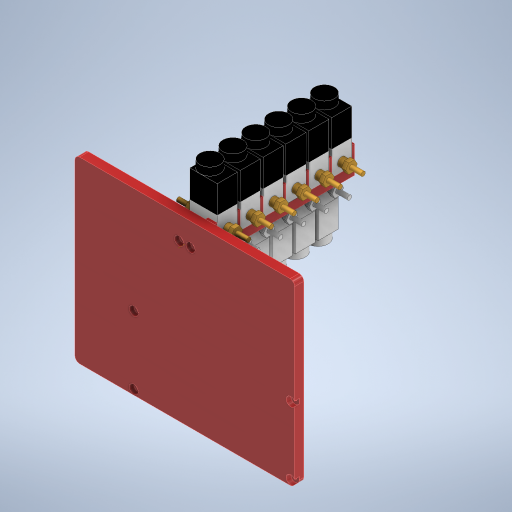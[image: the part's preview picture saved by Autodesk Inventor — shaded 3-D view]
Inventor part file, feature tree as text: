
AUTODESK INVENTOR PART (.ipt)
format: ipt  version: 2024.2 (Build 282272000, 272)  size: 1,256,960 bytes
history: native  units: mm
features: other x37, extrude x15, sketch x13, projected_geometry x11, mirror x2, pattern_linear x2, pattern_circular x2, plane x1, chamfer x1, fillet x1
ambient origin geometry x8: Origin, YZ Plane, XZ Plane, XY Plane, X Axis, Y Axis, Z Axis, Center Point
bodies: Solid6 (feature_tree), Solid8 (feature_tree), Solid11 (feature_tree), Solid14 (feature_tree), Solid17 (feature_tree), Solid20 (feature_tree), Solid7 (feature_tree), Solid10 (feature_tree), Solid13 (feature_tree), Solid16 (feature_tree), Solid19 (feature_tree), Solid9 (feature_tree), Solid12 (feature_tree), Solid15 (feature_tree), Solid18 (feature_tree), Solid21 (feature_tree), Solid48 (feature_tree), Solid53 (feature_tree), Solid47 (feature_tree), Solid52 (feature_tree), Solid46 (feature_tree), Solid51 (feature_tree), Solid45 (feature_tree), Solid50 (feature_tree), Solid44 (feature_tree), Solid49 (feature_tree), Solid42 (feature_tree), Solid41 (feature_tree), Solid43 (feature_tree), Solid54 (feature_tree), Solid55 (feature_tree), Solid56 (feature_tree), Solid57 (feature_tree), Solid58 (feature_tree)
feature tree (85):
  other  "Valvula P1"
  extrude  "Extrusion1"  Depth=30.0mm
  extrude  "Extrusion2"  Depth=5.0mm
  extrude  "Extrusion3"  Depth=27.0mm TaperAngle=0.0deg
  extrude  "Extrusion4"  Depth=8.5mm TaperAngle=0.0deg
  plane  "Work Plane1"
  mirror  "Mirror1"
  extrude  "Extrusion5"  Depth=10.0mm
  extrude  "Extrusion6"  Depth=11.4mm TaperAngle=0.0deg
  sketch  "Sketch7"  dims[d17=10.6mm d18=0.0mm d19=11.0mm]
  extrude  "Extrusion7"  Depth=11.0mm
  extrude  "Extrusion8"  Depth=4.6mm
  mirror  "Mirror2"
  pattern_linear  "Rectangular Pattern1"  Count1=6 Spacing1=25.0mm
  sketch  "Sketch9"  dims[d20=4.6mm d21=0.0mm d22=4.8mm]
  extrude  "Extrusion9"  Depth=10.0mm
  extrude  "Extrusion12"  Depth=6.0mm TaperAngle=0.0deg
  extrude  "Extrusion10"  Depth=20.0mm TaperAngle=360.0deg
  sketch  "Sketch12"  dims[d33=10.0mm d34=0.0mm d35=0.1mm]
  other  "Work Axis1"
  extrude  "Extrusion13"  Depth=0.05mm
  pattern_linear  "Rectangular Pattern2"  Spacing1=0.05mm  [1 undecoded]
  chamfer  "Chamfer2"  Distance=10.0mm
  pattern_circular  "Circular Pattern2"  Count=6  [1 undecoded]
  pattern_circular  "Circular Pattern3"  Count=2  [1 undecoded]
  extrude  "Extrusion14"  Depth=20.0mm TaperAngle=45.0deg
  extrude  "Extrusion17"  Depth=20.0mm TaperAngle=360.0deg
  extrude  "Extrusion18"  Depth=5.0mm
  fillet  "Fillet1"  Radius=12.5mm
  sketch  "Sketch1"  dims[d0=22.0mm d1=30.0mm]
  sketch  "Sketch2"  dims[d2=15.0mm d3=5.0mm]
  projected_geometry  "Projected Loop1"
  other  "Valvula P2"
  sketch  "Sketch3"  dims[d4=4.0mm d5=27.0mm d6=0.0mm]
  sketch  "Sketch4"  dims[d7=30.0mm d8=0.0mm d9=8.5mm d10=0.0mm]
  sketch  "Sketch5"  dims[d11=10.0mm d12=9.4mm]
  other  "Valvula P3"
  sketch  "Sketch6"  dims[d13=11.4mm d14=0.0mm d15=11.4mm d16=0.0mm]
  projected_geometry  "Projected Loop2"
  projected_geometry  "Projected Loop3"
  projected_geometry  "Projected Loop5"
  other  "Pattern of Valvula P2:1"
  other  "Pattern of Valvula P2:2"
  other  "Pattern of Valvula P2:3"
  other  "Pattern of Valvula P2:4"
  other  "Pattern of Valvula P2:5"
  other  "Pattern of Valvula P1:6"
  other  "Pattern of Valvula P1:7"
  other  "Pattern of Valvula P1:8"
  other  "Pattern of Valvula P1:9"
  other  "Pattern of Valvula P1:10"
  other  "Pattern of Valvula P3:11"
  other  "Pattern of Valvula P3:12"
  other  "Pattern of Valvula P3:13"
  other  "Pattern of Valvula P3:14"
  other  "Pattern of Valvula P3:15"
  projected_geometry  "Projected Loop11"
  projected_geometry  "Projected Loop12"
  projected_geometry  "Projected Loop13"
  projected_geometry  "Projected Loop14"
  projected_geometry  "Projected Loop15"
  sketch  "Sketch10"  dims[d23=12.7mm d24=0.0mm d25=60.0mm d27=25.0mm]
  projected_geometry  "Projected Loop16"
  sketch  "Sketch13"  dims[d36=3.0mm d44=6.0mm d45=0.0mm]
  other  "Pattern of Solid20:35"
  other  "Pattern of Solid19:36"
  other  "Pattern of Solid17:37"
  other  "Pattern of Solid16:38"
  other  "Pattern of Solid14:39"
  other  "Pattern of Solid13:40"
  other  "Pattern of Solid11:41"
  other  "Pattern of Solid10:42"
  other  "Pattern of Solid8:43"
  other  "Pattern of Solid7:44"
  other  "Pattern of Valvula P2:45"
  other  "Pattern of Valvula P1:46"
  other  "Pattern of Valvula P3:47"
  other  "Pattern of Solid9:48"
  other  "Pattern of Solid12:49"
  other  "Pattern of Solid15:50"
  other  "Pattern of Solid18:51"
  other  "Pattern of Solid21:52"
  sketch  "Sketch14"  dims[d59=0.0mm d60=0.0mm d61=20.0mm d62=360.0deg]
  sketch  "Sketch16"  dims[d64=7.3mm d65=0.05mm d66=0.05mm d67=10.0mm d68=0.0mm d69=60.0mm d71=25.0mm d72=20.0mm d73=20.0mm d74=2.0mm d75=45.0deg d76=20.0mm d77=360.0deg d79=5.0mm d80=12.5mm d81=10.0mm d82=0.0mm d83=3.0mm d84=20.0mm d86=25.0mm d88=74.0mm d89=171.5mm d90=3.3mm d91=180.0mm d92=85.0mm d93=107.0mm d95=3.3mm d96=3.3mm d105=2.0mm d106=195.5mm d107=15.0mm d108=240.0mm d109=10.0mm d110=0.0mm d111=58.0mm d112=10.0mm d113=5.0mm d114=0.0mm d115=5.0mm]
  projected_geometry  "Projected Loop18"
note: 3 required parameter values undecoded (feature->parameter linkage not recoverable at this tier; creation-order binding heuristic only, values carry confidence <= 0.55)
